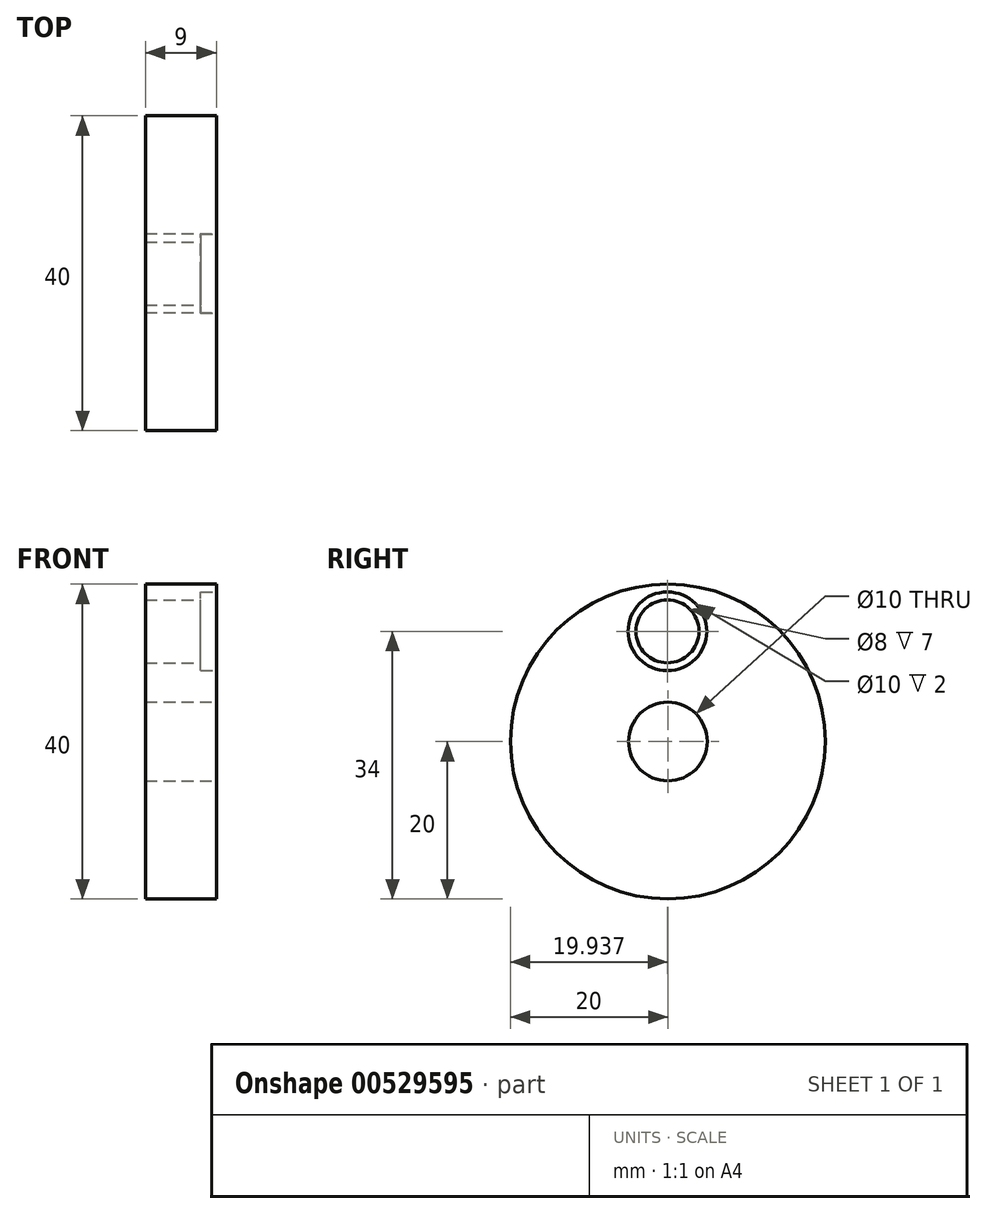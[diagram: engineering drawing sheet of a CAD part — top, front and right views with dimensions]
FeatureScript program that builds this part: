
annotation { "Feature Type Name" : "Feature", "Feature Type Description" : "" }
export const myFeature = defineFeature(function(context is Context, id is Id, definition is map)
    precondition{}
    {
        {
            var Q0;
            Q0=qCreatedBy(makeId("Right.planeOp"),FACE);
            var sketch = newSketch(context, id + "F0", { "sketchPlane" : qUnion([Q0])});
            skCircle(sketch, "E0", {"center": v(0, 0) * mm, "radius": 20 * mm});
            skSolve(sketch);
        }
        {
            var Q0;
            Q0 = qSketchRegion(id + "F0", true);
            extrude(context, id + "F1", {"entities" : qUnion([Q0]), "endBound" : BoundingType.SYMMETRIC, "depth" : 9 * mm, "offsetDistance" : 25 * mm});
        }
        {
            var Q0;
            Q0=makeQuery(id+"F1.opExtrude","CAP_FACE",FACE,{"disambiguationData":[OSD([sQuery(id+"F0.wireOp",EDGE,"E0")])],"isStart":false});
            var sketch = newSketch(context, id + "F2", { "sketchPlane" : qUnion([Q0])});
            skPoint(sketch, "E1", {"position": v(-0.06, 14) * mm});
            skPoint(sketch, "E2", {"position": v(0, 0) * mm});
            skSolve(sketch);
        }
        {
            var Q0;
            Q0=sQuery(id+"F2.wireOp",VERTEX,"E2");
            var Q1;
            Q1=makeQuery(id+"F1.opExtrude","SWEPT_BODY",BODY,{"disambiguationData":[OSD([sQuery(id+"F0.wireOp",EDGE,"E0")])]});
            hole(context, id + "F3", {"style" : HoleStyle.SIMPLE, "endStyle" : HoleEndStyle.THROUGH, "holeDiameter" : 10 * mm, "isTappedThrough" : true, "tappedDepth" : 12 * mm, "tapClearance" : 3, "locations" : qUnion([Q0]), "scope" : qUnion([Q1])});
        }
        {
            var Q0;
            Q0=sQuery(id+"F2.wireOp",VERTEX,"E1");
            var Q1;
            Q1=makeQuery(id+"F1.opExtrude","SWEPT_BODY",BODY,{"disambiguationData":[OSD([sQuery(id+"F0.wireOp",EDGE,"E0")])]});
            hole(context, id + "F4", {"style" : HoleStyle.C_BORE, "endStyle" : HoleEndStyle.THROUGH, "holeDiameter" : 8 * mm, "cBoreDiameter" : 10 * mm, "cBoreDepth" : 2 * mm, "isTappedThrough" : true, "tappedDepth" : 12 * mm, "tapClearance" : 3, "locations" : qUnion([Q0]), "scope" : qUnion([Q1])});
        }
    });
